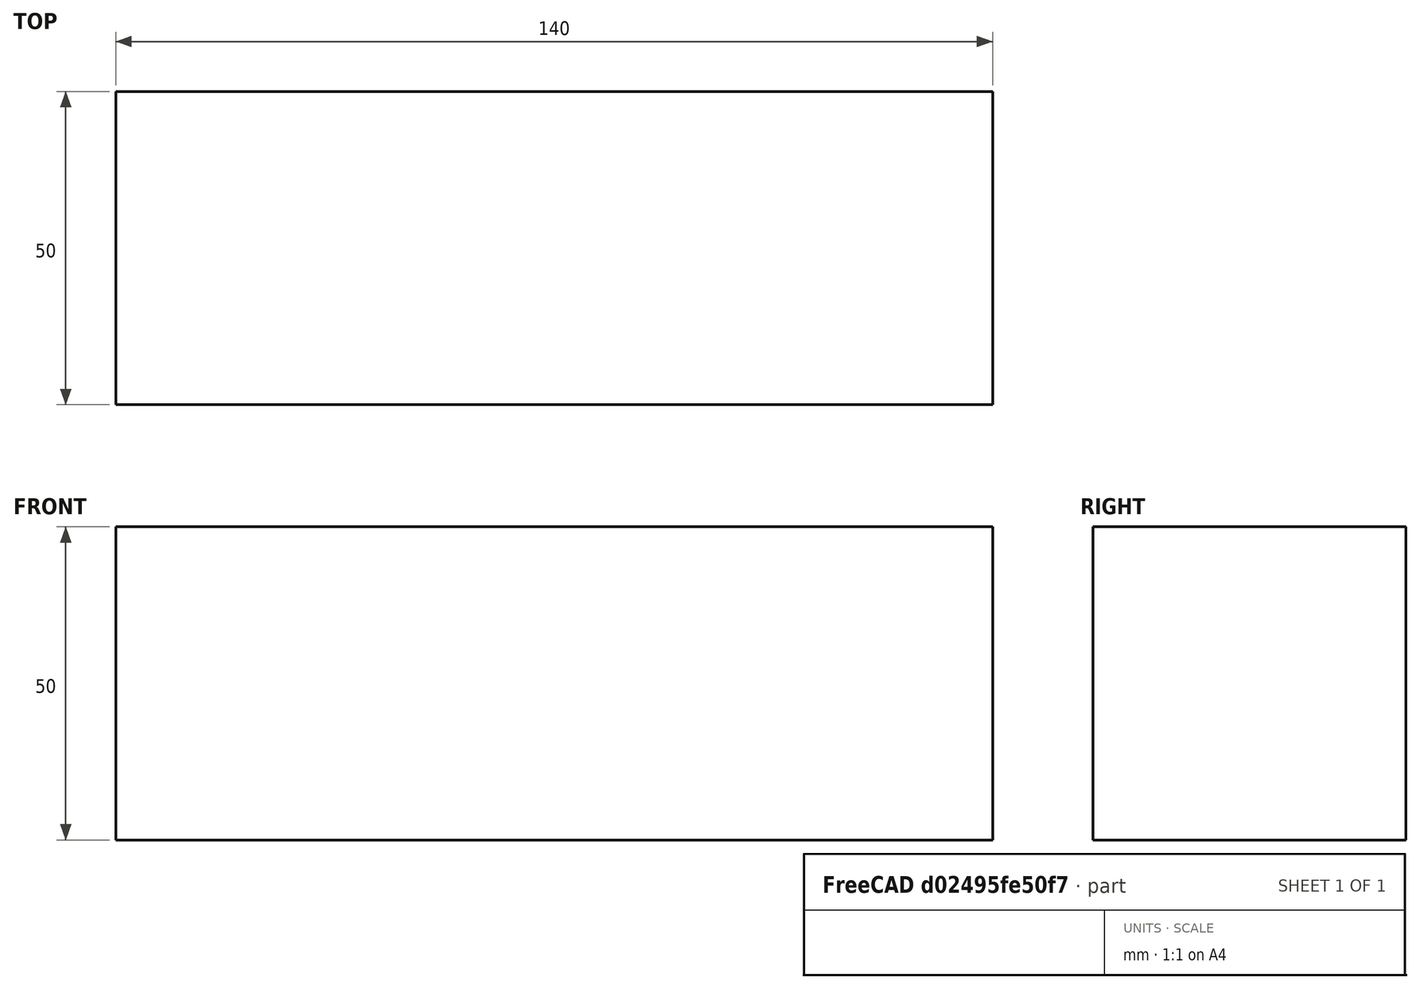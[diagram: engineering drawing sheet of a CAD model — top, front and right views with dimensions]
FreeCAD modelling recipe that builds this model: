
FCSTD DOCUMENT  (FreeCAD 0.15R4671 (Git))
Label: Flat Bar 140x50 EN10058 S235JR
License: All rights reserved
LicenseURL: http://en.wikipedia.org/wiki/All_rights_reserved
objects: Sketcher::SketchObject×1, Part::Extrusion×1
note: 2 computed .brp shape members not serialized (recipe doc carries the construction recipe); baked Part::Feature solids carry a one-line shape summary decoded from their .brp

FEATURE [Sketcher::SketchObject] Sketch
  sketch-geometry (4):
    g0: LineSegment StartX=-70 StartY=-25 StartZ=0 EndX=70 EndY=-25 EndZ=0
    g1: LineSegment StartX=70 StartY=-25 StartZ=0 EndX=70 EndY=25 EndZ=0
    g2: LineSegment StartX=70 StartY=25 StartZ=0 EndX=-70 EndY=25 EndZ=0
    g3: LineSegment StartX=-70 StartY=25 StartZ=0 EndX=-70 EndY=-25 EndZ=0
  constraints (12):
    c: Coincident(g0,g1)
    c: Coincident(g1,g2)
    c: Coincident(g2,g3)
    c: Coincident(g3,g0)
    c: Horizontal(g0)
    c: Horizontal(g2)
    c: Vertical(g1)
    c: Vertical(g3)
    c: Symmetric(g1,g2,g-2)
    c: Symmetric(g0,g1,g-1)
    c: DistanceY(g1) = 50
    c: DistanceX(g0) = 140
FEATURE [Part::Extrusion] Extrude  label="Flat Bar 140x50 EN10058 S235JR"
  Base = -> Sketch
  Dir = (0,0,50)
  Solid = true
